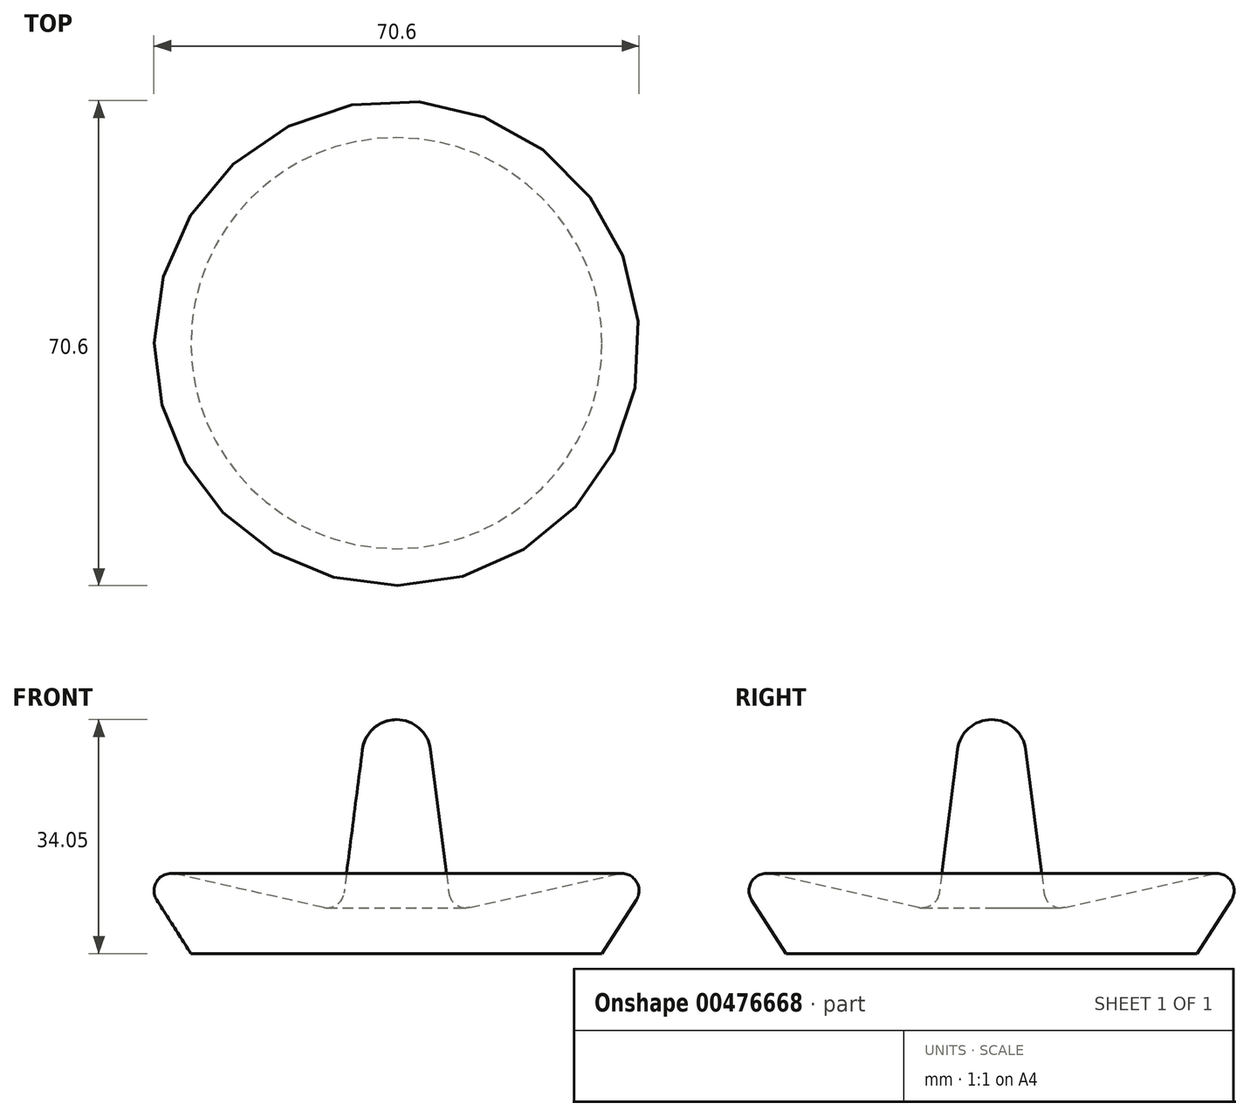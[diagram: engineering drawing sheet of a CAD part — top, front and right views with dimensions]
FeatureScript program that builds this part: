
annotation { "Feature Type Name" : "Feature", "Feature Type Description" : "" }
export const myFeature = defineFeature(function(context is Context, id is Id, definition is map)
    precondition{}
    {
        {
            var Q0;
            Q0=qCreatedBy(makeId("Front.planeOp"),FACE);
            var sketch = newSketch(context, id + "F0", { "sketchPlane" : qUnion([Q0])});
            skArc(sketch, "E0", {"start": v(0, 34.05) * mm, "mid": v(-3.3, 32.8) * mm, "end": v(-4.96, 29.69) * mm});
            skArc(sketch, "E1", {"start": v(-32.25, 11.59) * mm, "mid": v(-34.84, 10.59) * mm, "end": v(-34.9, 7.8) * mm});
            skArc(sketch, "E2", {"start": v(-10.66, 6.71) * mm, "mid": v(-8.67, 7.1) * mm, "end": v(-7.63, 8.83) * mm});
            skLineSegment(sketch, "E3", {"start": v(-4.96, 29.69) * mm, "end": v(-7.63, 8.83) * mm});
            skLineSegment(sketch, "E4", {"start": v(-29.92, 0) * mm, "end": v(0, 0) * mm});
            skLineSegment(sketch, "E5", {"start": v(0, 0) * mm, "end": v(0, 34.05) * mm});
            skLineSegment(sketch, "E6", {"start": v(-10.66, 6.71) * mm, "end": v(-32.25, 11.59) * mm});
            skLineSegment(sketch, "E7", {"start": v(-34.9, 7.8) * mm, "end": v(-29.92, 0) * mm});
            skSolve(sketch);
        }
        {
            var Q0;
            Q0=makeQuery(id+"F0.imprint","IMPRINT",FACE,{"disambiguationData":[TD([[makeQuery(id+"F0.imprint","IMPRINT",EDGE,{"derivedFrom":sQuery(id+"F0.wireOp",EDGE,"E0")}),1.0]])]});
            var Q1;
            Q1=sQuery(id+"F0.wireOp",EDGE,"E5");
            revolve(context, id + "F1", {"entities" : qUnion([Q0]), "axis" : qUnion([Q1]), "revolveType" : RevolveType.FULL});
        }
    });
